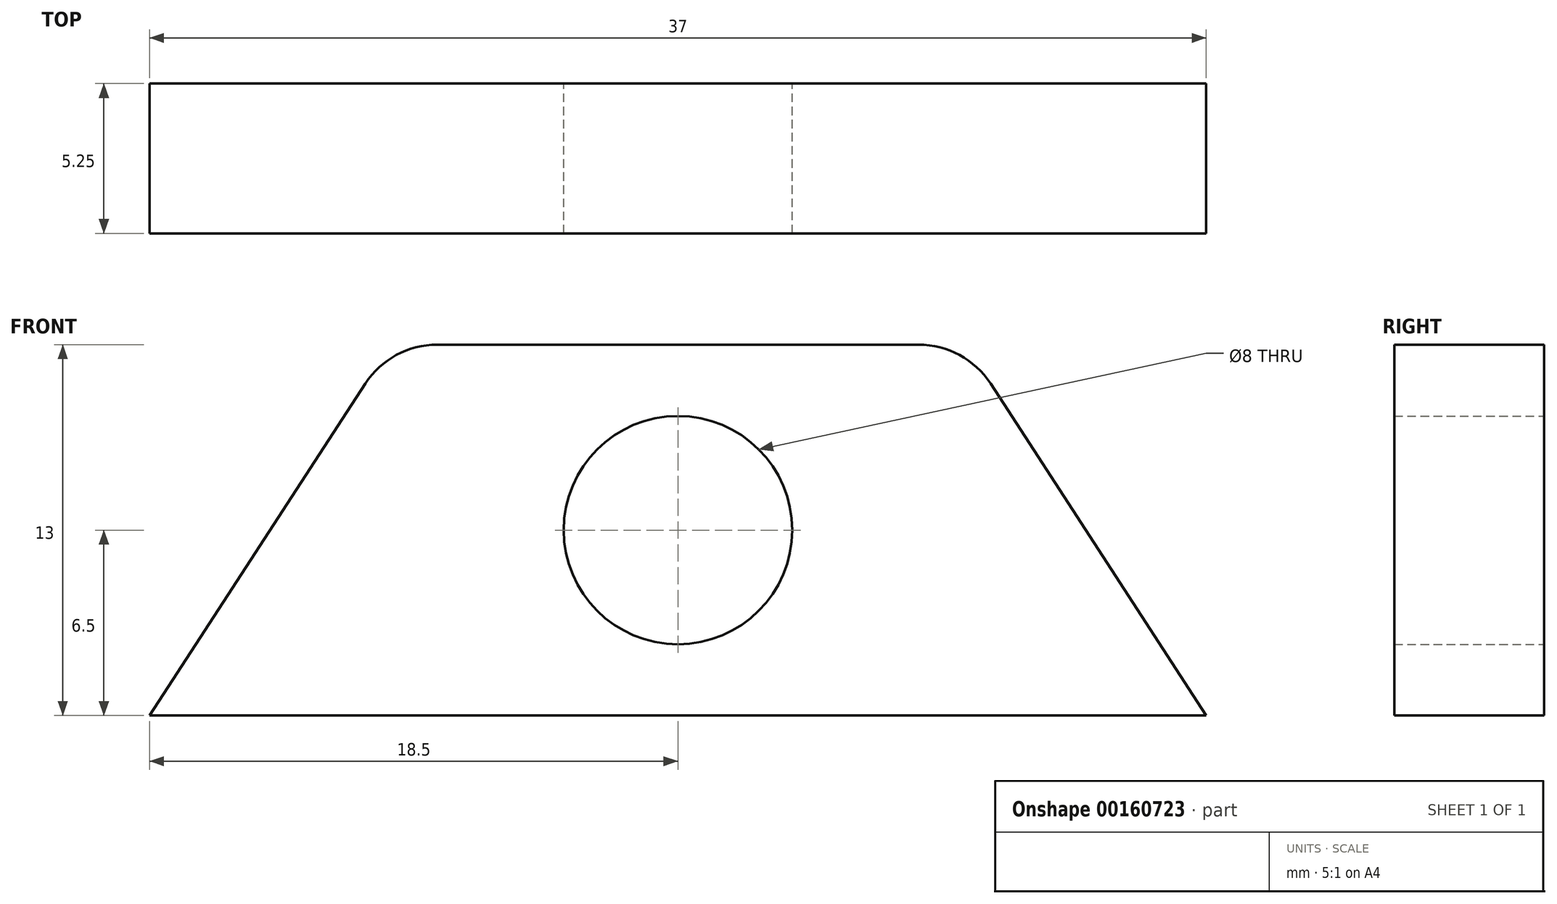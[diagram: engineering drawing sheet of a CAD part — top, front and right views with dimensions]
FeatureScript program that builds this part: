
annotation { "Feature Type Name" : "Feature", "Feature Type Description" : "" }
export const myFeature = defineFeature(function(context is Context, id is Id, definition is map)
    precondition{}
    {
        {
            var Q0;
            Q0=qCreatedBy(makeId("Front.planeOp"),FACE);
            var sketch = newSketch(context, id + "F0", { "sketchPlane" : qUnion([Q0])});
            skLineSegment(sketch, "E0.bottom", {"start": v(0, 0) * mm, "end": v(37, 0) * mm});
            skLineSegment(sketch, "E0.top", {"start": v(8.44, 13) * mm, "end": v(28.56, 13) * mm});
            skLineSegment(sketch, "E1", {"start": v(0, 0) * mm, "end": v(8.44, 13) * mm});
            skLineSegment(sketch, "E2", {"start": v(28.56, 13) * mm, "end": v(37, 0) * mm});
            skCircle(sketch, "E3", {"center": v(18.5, 6.5) * mm, "radius": 4 * mm});
            skPoint(sketch, "E3.centerSnap0", {"position": v(18.5, 13) * mm});
            skLineSegment(sketch, "E4", {"start": v(18.5, 2.5) * mm, "end": v(18.5, 10.5) * mm, "construction": true});
            skSolve(sketch);
        }
        {
            var Q0;
            Q0 = qSketchRegion(id + "F0", true);
            extrude(context, id + "F1", {"entities" : qUnion([Q0]), "depth" : 5.25 * mm});
        }
        {
            var Q0;
            Q0=makeQuery(id+"F1.opExtrude","SWEPT_EDGE",EDGE,{"disambiguationData":[OSD([sQuery(id+"F0.wireOp",EDGE,"E0.top"),sQuery(id+"F0.wireOp",EDGE,"E1")])]});
            var Q1;
            Q1=makeQuery(id+"F1.opExtrude","SWEPT_EDGE",EDGE,{"disambiguationData":[OSD([sQuery(id+"F0.wireOp",EDGE,"E0.top"),sQuery(id+"F0.wireOp",EDGE,"E2")])]});
            fillet(context, id + "F2", {"entities" : qUnion([Q0, Q1]), "radius" : 3 * mm, "tangentPropagation" : true, "allowEdgeOverflow" : false});
        }
    });
